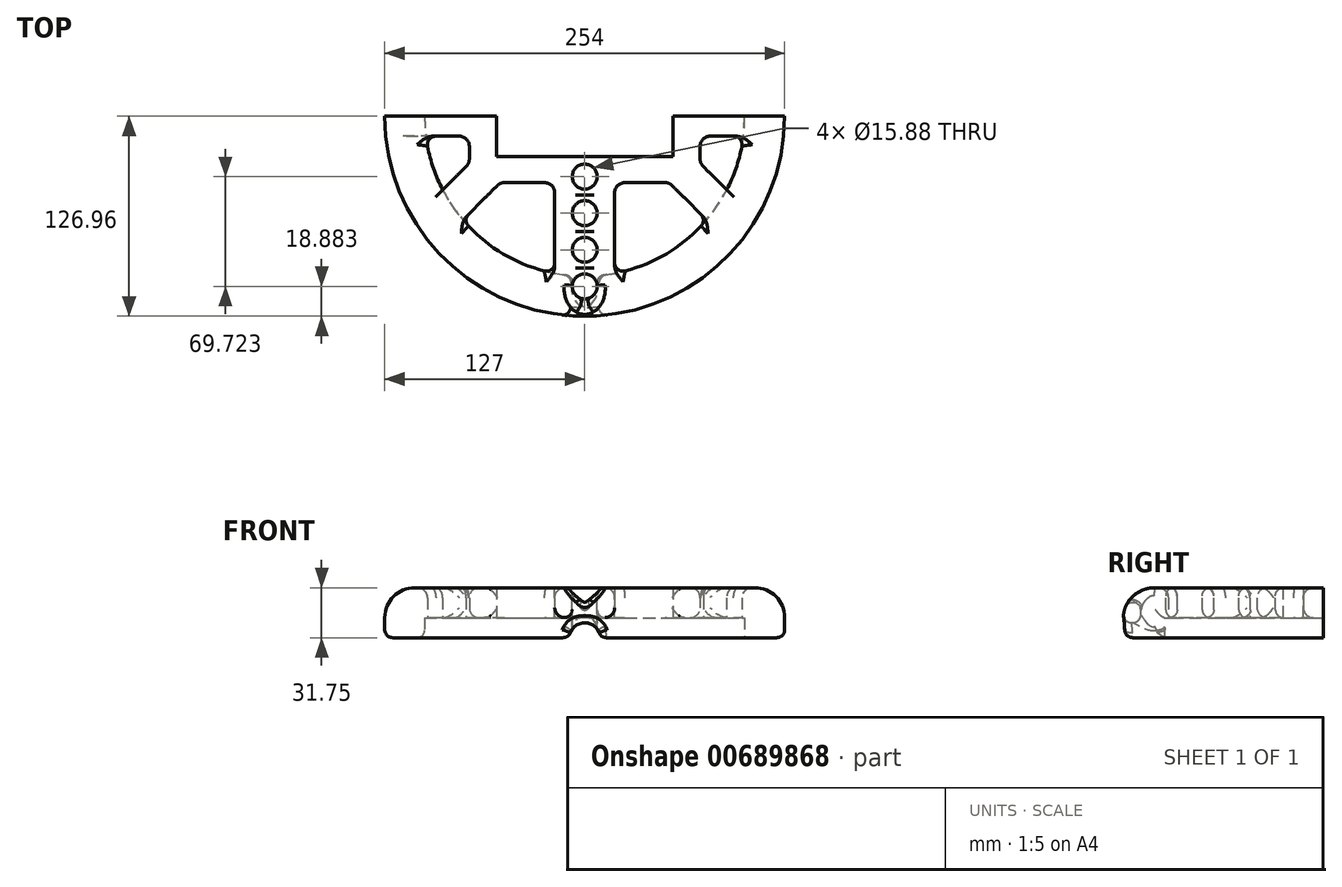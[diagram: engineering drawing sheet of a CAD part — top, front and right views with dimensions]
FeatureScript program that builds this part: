
annotation { "Feature Type Name" : "Feature", "Feature Type Description" : "" }
export const myFeature = defineFeature(function(context is Context, id is Id, definition is map)
    precondition{}
    {
        {
            var Q0;
            Q0=qCreatedBy(makeId("Top.planeOp"),FACE);
            var sketch = newSketch(context, id + "F0", { "sketchPlane" : qUnion([Q0])});
            skCircle(sketch, "E0", {"center": v(0, 0) * mm, "radius": 127 * mm});
            skCircle(sketch, "E1", {"center": v(0, 0) * mm, "radius": 101.6 * mm});
            skLineSegment(sketch, "E2", {"start": v(-127, 0) * mm, "end": v(127, 0) * mm});
            skLineSegment(sketch, "E3.bottom", {"start": v(-56.13, -25.65) * mm, "end": v(56.13, -25.65) * mm});
            skLineSegment(sketch, "E3.top", {"start": v(-56.13, 25.65) * mm, "end": v(56.13, 25.65) * mm});
            skLineSegment(sketch, "E3.left", {"start": v(-56.13, -25.65) * mm, "end": v(-56.13, 25.65) * mm});
            skLineSegment(sketch, "E3.right", {"start": v(56.13, -25.65) * mm, "end": v(56.13, 25.65) * mm});
            skLineSegment(sketch, "E4", {"start": v(-56.13, -12.7) * mm, "end": v(-100.8, -12.7) * mm});
            skLineSegment(sketch, "E5", {"start": v(0, 25.65) * mm, "end": v(0, -25.65) * mm, "construction": true});
            skLineSegment(sketch, "E6", {"start": v(0, 0) * mm, "end": v(-89.8, -89.8) * mm, "construction": true});
            skLineSegment(sketch, "E7", {"start": v(-56.13, -12.7) * mm, "end": v(-90.2, -46.76) * mm});
            skPoint(sketch, "E8", {"position": v(-37.08, -25.65) * mm});
            skLineSegment(sketch, "E9", {"start": v(-37.08, -25.65) * mm, "end": v(-77.33, -65.9) * mm});
            skLineSegment(sketch, "E10.bottom", {"start": v(-73.28, -42.16) * mm, "end": v(73.28, -42.16) * mm});
            skLineSegment(sketch, "E10.top", {"start": v(-73.28, 42.16) * mm, "end": v(73.28, 42.16) * mm});
            skLineSegment(sketch, "E10.left", {"start": v(-73.28, -42.16) * mm, "end": v(-73.28, 42.16) * mm});
            skLineSegment(sketch, "E10.right", {"start": v(73.28, -42.16) * mm, "end": v(73.28, 42.16) * mm});
            skLineSegment(sketch, "E11.MirrorCS", {"start": v(37.08, -25.65) * mm, "end": v(77.33, -65.9) * mm});
            skLineSegment(sketch, "E12.MirrorCS", {"start": v(56.13, -12.7) * mm, "end": v(90.2, -46.76) * mm});
            skLineSegment(sketch, "E13.MirrorCS", {"start": v(56.13, -12.7) * mm, "end": v(100.8, -12.7) * mm});
            skLineSegment(sketch, "E14", {"start": v(-19.05, -42.16) * mm, "end": v(-19.05, -99.8) * mm});
            skLineSegment(sketch, "E15.MirrorCS", {"start": v(19.05, -42.16) * mm, "end": v(19.05, -99.8) * mm});
            skSolve(sketch);
        }
        {
            var Q0;
            {var subQ0=sQuery(id+"F0.wireOp",EDGE,"E2");var subQ1=sQuery(id+"F0.wireOp",EDGE,"E0");var subQ2=makeQuery(id+"F0.imprint","INTERSECT",VERTEX,{"disambiguationData":[OD(0.0)],"derivedFrom":[subQ1,subQ0]});Q0=makeQuery(id+"F0.imprint","IMPRINT",FACE,{"disambiguationData":[TD([[makeQuery(id+"F0.imprint","IMPRINT",EDGE,{"disambiguationData":[TD([[subQ2,-1.0]])],"derivedFrom":subQ1}),1.0]])]});}
            var Q1;
            {var subQ0=sQuery(id+"F0.wireOp",EDGE,"E4");var subQ1=sQuery(id+"F0.wireOp",EDGE,"E1");var subQ2=makeQuery(id+"F0.imprint","INTERSECT",VERTEX,{"derivedFrom":[subQ1,subQ0]});Q1=makeQuery(id+"F0.imprint","IMPRINT",FACE,{"disambiguationData":[TD([[makeQuery(id+"F0.imprint","IMPRINT",EDGE,{"disambiguationData":[TD([[subQ2,1.0]])],"derivedFrom":subQ1}),1.0]])]});}
            var Q2;
            {var subQ0=sQuery(id+"F0.wireOp",EDGE,"E10.left");var subQ1=sQuery(id+"F0.wireOp",EDGE,"E2");var subQ2=makeQuery(id+"F0.imprint","INTERSECT",VERTEX,{"derivedFrom":[subQ1,subQ0]});Q2=makeQuery(id+"F0.imprint","IMPRINT",FACE,{"disambiguationData":[TD([[makeQuery(id+"F0.imprint","IMPRINT",EDGE,{"disambiguationData":[TD([[subQ2,-1.0]])],"derivedFrom":subQ1}),-1.0]])]});}
            var Q3;
            {var subQ1=sQuery(id+"F0.wireOp",EDGE,"E4");var subQ3=sQuery(id+"F0.wireOp",EDGE,"E10.left");var subQ4=makeQuery(id+"F0.imprint","INTERSECT",VERTEX,{"derivedFrom":[subQ1,subQ3]});Q3=makeQuery(id+"F0.imprint","IMPRINT",FACE,{"disambiguationData":[TD([[makeQuery(id+"F0.imprint","IMPRINT",EDGE,{"disambiguationData":[TD([[subQ4,1.0]])],"derivedFrom":subQ3}),-1.0]])]});}
            var Q4;
            {var subQ1=sQuery(id+"F0.wireOp",EDGE,"E3.left");var subQ6=sQuery(id+"F0.wireOp",EDGE,"E3.bottom");var subQ10=makeQuery(id+"F0.imprint","INTERSECT",VERTEX,{"derivedFrom":[subQ6,subQ1]});Q4=makeQuery(id+"F0.imprint","IMPRINT",FACE,{"disambiguationData":[TD([[makeQuery(id+"F0.imprint","IMPRINT",EDGE,{"disambiguationData":[TD([[subQ10,-1.0]])],"derivedFrom":subQ6}),-1.0]])]});}
            var Q5;
            {var subQ0=sQuery(id+"F0.wireOp",EDGE,"E9");var subQ1=sQuery(id+"F0.wireOp",EDGE,"E3.bottom");var subQ2=makeQuery(id+"F0.imprint","INTERSECT",VERTEX,{"derivedFrom":[subQ1,subQ0]});Q5=makeQuery(id+"F0.imprint","IMPRINT",FACE,{"disambiguationData":[TD([[makeQuery(id+"F0.imprint","IMPRINT",EDGE,{"disambiguationData":[TD([[subQ2,-1.0]])],"derivedFrom":subQ1}),-1.0]])]});}
            var Q6;
            {var subQ5=sQuery(id+"F0.wireOp",EDGE,"E3.right");var subQ6=sQuery(id+"F0.wireOp",EDGE,"E3.bottom");var subQ7=makeQuery(id+"F0.imprint","INTERSECT",VERTEX,{"derivedFrom":[subQ6,subQ5]});Q6=makeQuery(id+"F0.imprint","IMPRINT",FACE,{"disambiguationData":[TD([[makeQuery(id+"F0.imprint","IMPRINT",EDGE,{"disambiguationData":[TD([[subQ7,1.0]])],"derivedFrom":subQ6}),-1.0]])]});}
            var Q7;
            {var subQ0=sQuery(id+"F0.wireOp",EDGE,"E12.MirrorCS");var subQ1=sQuery(id+"F0.wireOp",EDGE,"E10.right");var subQ2=makeQuery(id+"F0.imprint","INTERSECT",VERTEX,{"derivedFrom":[subQ1,subQ0]});Q7=makeQuery(id+"F0.imprint","IMPRINT",FACE,{"disambiguationData":[TD([[makeQuery(id+"F0.imprint","IMPRINT",EDGE,{"disambiguationData":[TD([[subQ2,-1.0]])],"derivedFrom":subQ1}),1.0]])]});}
            var Q8;
            {var subQ0=sQuery(id+"F0.wireOp",EDGE,"E3.right");var subQ1=sQuery(id+"F0.wireOp",EDGE,"E2");var subQ2=makeQuery(id+"F0.imprint","INTERSECT",VERTEX,{"derivedFrom":[subQ1,subQ0]});Q8=makeQuery(id+"F0.imprint","IMPRINT",FACE,{"disambiguationData":[TD([[makeQuery(id+"F0.imprint","IMPRINT",EDGE,{"disambiguationData":[TD([[subQ2,-1.0]])],"derivedFrom":subQ1}),-1.0]])]});}
            var Q9;
            {var subQ0=sQuery(id+"F0.wireOp",EDGE,"E13.MirrorCS");var subQ1=sQuery(id+"F0.wireOp",EDGE,"E1");var subQ2=makeQuery(id+"F0.imprint","INTERSECT",VERTEX,{"derivedFrom":[subQ1,subQ0]});Q9=makeQuery(id+"F0.imprint","IMPRINT",FACE,{"disambiguationData":[TD([[makeQuery(id+"F0.imprint","IMPRINT",EDGE,{"disambiguationData":[TD([[subQ2,-1.0]])],"derivedFrom":subQ1}),1.0]])]});}
            var Q10;
            {var subQ5=sQuery(id+"F0.wireOp",EDGE,"E1");var subQ7=sQuery(id+"F0.wireOp",EDGE,"E7");var subQ8=makeQuery(id+"F0.imprint","INTERSECT",VERTEX,{"derivedFrom":[subQ5,subQ7]});Q10=makeQuery(id+"F0.imprint","IMPRINT",FACE,{"disambiguationData":[TD([[makeQuery(id+"F0.imprint","IMPRINT",EDGE,{"disambiguationData":[TD([[subQ8,-1.0]])],"derivedFrom":subQ5}),1.0]])]});}
            var Q11;
            {var subQ0=sQuery(id+"F0.wireOp",EDGE,"E11.MirrorCS");var subQ1=sQuery(id+"F0.wireOp",EDGE,"E1");var subQ2=makeQuery(id+"F0.imprint","INTERSECT",VERTEX,{"derivedFrom":[subQ1,subQ0]});Q11=makeQuery(id+"F0.imprint","IMPRINT",FACE,{"disambiguationData":[TD([[makeQuery(id+"F0.imprint","IMPRINT",EDGE,{"disambiguationData":[TD([[subQ2,-1.0]])],"derivedFrom":subQ1}),1.0]])]});}
            var Q12;
            {var subQ0=sQuery(id+"F0.wireOp",EDGE,"E14");Q12=makeQuery(id+"F0.imprint","IMPRINT",FACE,{"disambiguationData":[TD([[makeQuery(id+"F0.imprint","IMPRINT",EDGE,{"derivedFrom":subQ0}),1.0]])]});}
            extrude(context, id + "F1", {"entities" : qUnion([Q0, Q1, Q2, Q3, Q4, Q5, Q6, Q7, Q8, Q9, Q10, Q11, Q12]), "depth" : 31.75 * mm, "offsetDistance" : 25.4 * mm});
        }
        {
            var Q0;
            Q0=qCreatedBy(makeId("Front.planeOp"),FACE);
            cPlane(context, id + "F2", {"entities" : qUnion([Q0]), "cplaneType" : CPlaneType.OFFSET, "offset" : 139.7 * mm, "width" : 152.4 * mm, "height" : 152.4 * mm});
        }
        {
            var Q0;
            Q0=qCreatedBy(id+"F2.planeOp",FACE);
            var sketch = newSketch(context, id + "F3", { "sketchPlane" : qUnion([Q0])});
            skCircle(sketch, "E16", {"center": v(0, 0) * mm, "radius": 9.53 * mm});
            skSolve(sketch);
        }
        {
            var Q0;
            Q0=makeQuery(id+"F3.imprint","IMPRINT",FACE,{"disambiguationData":[TD([[makeQuery(id+"F3.imprint","IMPRINT",EDGE,{"derivedFrom":sQuery(id+"F3.wireOp",EDGE,"E16")}),1.0]])]});
            extrude(context, id + "F4", {"entities" : qUnion([Q0]), "operationType" : NewBodyOperationType.REMOVE, "oppositeDirection" : true, "depth" : 44.45 * mm, "offsetDistance" : 25.4 * mm});
        }
        {
            var Q0;
            {var subQ0=sQuery(id+"F0.wireOp",EDGE,"E14");Q0=makeQuery(id+"F0.imprint","IMPRINT",FACE,{"disambiguationData":[TD([[makeQuery(id+"F0.imprint","IMPRINT",EDGE,{"derivedFrom":subQ0}),1.0]])]});}
            var Q1;
            {var subQ0=sQuery(id+"F0.wireOp",EDGE,"E11.MirrorCS");var subQ1=sQuery(id+"F0.wireOp",EDGE,"E1");var subQ2=makeQuery(id+"F0.imprint","INTERSECT",VERTEX,{"derivedFrom":[subQ1,subQ0]});Q1=makeQuery(id+"F0.imprint","IMPRINT",FACE,{"disambiguationData":[TD([[makeQuery(id+"F0.imprint","IMPRINT",EDGE,{"disambiguationData":[TD([[subQ2,-1.0]])],"derivedFrom":subQ1}),1.0]])]});}
            var Q2;
            {var subQ7=sQuery(id+"F0.wireOp",EDGE,"E3.right");var subQ8=sQuery(id+"F0.wireOp",EDGE,"E3.bottom");var subQ9=makeQuery(id+"F0.imprint","INTERSECT",VERTEX,{"derivedFrom":[subQ8,subQ7]});Q2=makeQuery(id+"F0.imprint","IMPRINT",FACE,{"disambiguationData":[TD([[makeQuery(id+"F0.imprint","IMPRINT",EDGE,{"disambiguationData":[TD([[subQ9,1.0]])],"derivedFrom":subQ8}),-1.0]])]});}
            var Q3;
            {var subQ0=sQuery(id+"F0.wireOp",EDGE,"E12.MirrorCS");var subQ1=sQuery(id+"F0.wireOp",EDGE,"E10.right");var subQ2=makeQuery(id+"F0.imprint","INTERSECT",VERTEX,{"derivedFrom":[subQ1,subQ0]});Q3=makeQuery(id+"F0.imprint","IMPRINT",FACE,{"disambiguationData":[TD([[makeQuery(id+"F0.imprint","IMPRINT",EDGE,{"disambiguationData":[TD([[subQ2,-1.0]])],"derivedFrom":subQ1}),1.0]])]});}
            var Q4;
            {var subQ0=sQuery(id+"F0.wireOp",EDGE,"E3.right");var subQ1=sQuery(id+"F0.wireOp",EDGE,"E2");var subQ2=makeQuery(id+"F0.imprint","INTERSECT",VERTEX,{"derivedFrom":[subQ1,subQ0]});Q4=makeQuery(id+"F0.imprint","IMPRINT",FACE,{"disambiguationData":[TD([[makeQuery(id+"F0.imprint","IMPRINT",EDGE,{"disambiguationData":[TD([[subQ2,-1.0]])],"derivedFrom":subQ1}),-1.0]])]});}
            var Q5;
            {var subQ0=sQuery(id+"F0.wireOp",EDGE,"E13.MirrorCS");var subQ1=sQuery(id+"F0.wireOp",EDGE,"E1");var subQ2=makeQuery(id+"F0.imprint","INTERSECT",VERTEX,{"derivedFrom":[subQ1,subQ0]});Q5=makeQuery(id+"F0.imprint","IMPRINT",FACE,{"disambiguationData":[TD([[makeQuery(id+"F0.imprint","IMPRINT",EDGE,{"disambiguationData":[TD([[subQ2,-1.0]])],"derivedFrom":subQ1}),1.0]])]});}
            var Q6;
            {var subQ3=sQuery(id+"F0.wireOp",EDGE,"E9");var subQ5=sQuery(id+"F0.wireOp",EDGE,"E3.bottom");var subQ6=makeQuery(id+"F0.imprint","INTERSECT",VERTEX,{"derivedFrom":[subQ5,subQ3]});Q6=makeQuery(id+"F0.imprint","IMPRINT",FACE,{"disambiguationData":[TD([[makeQuery(id+"F0.imprint","IMPRINT",EDGE,{"disambiguationData":[TD([[subQ6,-1.0]])],"derivedFrom":subQ5}),-1.0]])]});}
            var Q7;
            {var subQ1=sQuery(id+"F0.wireOp",EDGE,"E3.left");var subQ6=sQuery(id+"F0.wireOp",EDGE,"E3.bottom");var subQ10=makeQuery(id+"F0.imprint","INTERSECT",VERTEX,{"derivedFrom":[subQ6,subQ1]});Q7=makeQuery(id+"F0.imprint","IMPRINT",FACE,{"disambiguationData":[TD([[makeQuery(id+"F0.imprint","IMPRINT",EDGE,{"disambiguationData":[TD([[subQ10,-1.0]])],"derivedFrom":subQ6}),-1.0]])]});}
            var Q8;
            {var subQ1=sQuery(id+"F0.wireOp",EDGE,"E1");var subQ5=sQuery(id+"F0.wireOp",EDGE,"E7");var subQ6=makeQuery(id+"F0.imprint","INTERSECT",VERTEX,{"derivedFrom":[subQ1,subQ5]});Q8=makeQuery(id+"F0.imprint","IMPRINT",FACE,{"disambiguationData":[TD([[makeQuery(id+"F0.imprint","IMPRINT",EDGE,{"disambiguationData":[TD([[subQ6,-1.0]])],"derivedFrom":subQ1}),1.0]])]});}
            var Q9;
            {var subQ0=sQuery(id+"F0.wireOp",EDGE,"E4");var subQ1=sQuery(id+"F0.wireOp",EDGE,"E1");var subQ2=makeQuery(id+"F0.imprint","INTERSECT",VERTEX,{"derivedFrom":[subQ1,subQ0]});Q9=makeQuery(id+"F0.imprint","IMPRINT",FACE,{"disambiguationData":[TD([[makeQuery(id+"F0.imprint","IMPRINT",EDGE,{"disambiguationData":[TD([[subQ2,1.0]])],"derivedFrom":subQ1}),1.0]])]});}
            var Q10;
            {var subQ1=sQuery(id+"F0.wireOp",EDGE,"E4");var subQ3=sQuery(id+"F0.wireOp",EDGE,"E10.left");var subQ4=makeQuery(id+"F0.imprint","INTERSECT",VERTEX,{"derivedFrom":[subQ1,subQ3]});Q10=makeQuery(id+"F0.imprint","IMPRINT",FACE,{"disambiguationData":[TD([[makeQuery(id+"F0.imprint","IMPRINT",EDGE,{"disambiguationData":[TD([[subQ4,1.0]])],"derivedFrom":subQ3}),-1.0]])]});}
            var Q11;
            {var subQ0=sQuery(id+"F0.wireOp",EDGE,"E10.left");var subQ1=sQuery(id+"F0.wireOp",EDGE,"E2");var subQ2=makeQuery(id+"F0.imprint","INTERSECT",VERTEX,{"derivedFrom":[subQ1,subQ0]});Q11=makeQuery(id+"F0.imprint","IMPRINT",FACE,{"disambiguationData":[TD([[makeQuery(id+"F0.imprint","IMPRINT",EDGE,{"disambiguationData":[TD([[subQ2,-1.0]])],"derivedFrom":subQ1}),-1.0]])]});}
            extrude(context, id + "F5", {"entities" : qUnion([Q0, Q1, Q2, Q3, Q4, Q5, Q6, Q7, Q8, Q9, Q10, Q11]), "operationType" : NewBodyOperationType.REMOVE, "depth" : 12.7 * mm, "offsetDistance" : 25.4 * mm});
        }
        {
            var Q0;
            Q0=makeQuery(id+"FQLxLcLUYKDh7PT_1.6.F4.boolean.opBoolean","COPY",FACE,{"derivedFrom":makeQuery(id+"FQLxLcLUYKDh7PT_1.6.F4.opExtrude","SWEPT_FACE",FACE,{"disambiguationData":[OSD([sQuery(id+"F3.wireOp",EDGE,"E16")])]})});
            var Q1;
            Q1=makeQuery(id+"FQLxLcLUYKDh7PT_1.7.F4.boolean.opBoolean","COPY",FACE,{"derivedFrom":makeQuery(id+"FQLxLcLUYKDh7PT_1.7.F4.opExtrude","SWEPT_FACE",FACE,{"disambiguationData":[OSD([sQuery(id+"F3.wireOp",EDGE,"E16")])]})});
            var Q2;
            Q2=makeQuery(id+"FQLxLcLUYKDh7PT_1.5.F4.boolean.opBoolean","COPY",FACE,{"derivedFrom":makeQuery(id+"FQLxLcLUYKDh7PT_1.5.F4.opExtrude","SWEPT_FACE",FACE,{"disambiguationData":[OSD([sQuery(id+"F3.wireOp",EDGE,"E16")])]})});
            var Q3;
            Q3=makeQuery(id+"FQLxLcLUYKDh7PT_1.4.F4.boolean.opBoolean","COPY",FACE,{"derivedFrom":makeQuery(id+"FQLxLcLUYKDh7PT_1.4.F4.opExtrude","SWEPT_FACE",FACE,{"disambiguationData":[OSD([sQuery(id+"F3.wireOp",EDGE,"E16")])]})});
            var Q4;
            Q4=makeQuery(id+"FQLxLcLUYKDh7PT_1.3.F4.boolean.opBoolean","COPY",FACE,{"derivedFrom":makeQuery(id+"FQLxLcLUYKDh7PT_1.3.F4.opExtrude","SWEPT_FACE",FACE,{"disambiguationData":[OSD([sQuery(id+"F3.wireOp",EDGE,"E16")])]})});
            var Q5;
            Q5=makeQuery(id+"FQLxLcLUYKDh7PT_1.2.F4.boolean.opBoolean","COPY",FACE,{"derivedFrom":makeQuery(id+"FQLxLcLUYKDh7PT_1.2.F4.opExtrude","SWEPT_FACE",FACE,{"disambiguationData":[OSD([sQuery(id+"F3.wireOp",EDGE,"E16")])]})});
            var Q6;
            Q6=makeQuery(id+"FQLxLcLUYKDh7PT_1.1.F4.boolean.opBoolean","COPY",FACE,{"derivedFrom":makeQuery(id+"FQLxLcLUYKDh7PT_1.1.F4.opExtrude","SWEPT_FACE",FACE,{"disambiguationData":[OSD([sQuery(id+"F3.wireOp",EDGE,"E16")])]})});
            var Q7;
            Q7=makeQuery(id+"F4.boolean.opBoolean","COPY",FACE,{"derivedFrom":makeQuery(id+"F4.opExtrude","SWEPT_FACE",FACE,{"disambiguationData":[OSD([sQuery(id+"F3.wireOp",EDGE,"E16")])]})});
            var Q8;
            Q8=makeQuery(id+"FQLxLcLUYKDh7PT_1.-1.F4.boolean.opBoolean","COPY",FACE,{"derivedFrom":makeQuery(id+"FQLxLcLUYKDh7PT_1.-1.F4.opExtrude","SWEPT_FACE",FACE,{"disambiguationData":[OSD([sQuery(id+"F3.wireOp",EDGE,"E16")])]})});
            var Q9;
            Q9=makeQuery(id+"FQLxLcLUYKDh7PT_1.-2.F4.boolean.opBoolean","COPY",FACE,{"derivedFrom":makeQuery(id+"FQLxLcLUYKDh7PT_1.-2.F4.opExtrude","SWEPT_FACE",FACE,{"disambiguationData":[OSD([sQuery(id+"F3.wireOp",EDGE,"E16")])]})});
            var Q10;
            Q10=makeQuery(id+"FQLxLcLUYKDh7PT_1.-3.F4.boolean.opBoolean","COPY",FACE,{"derivedFrom":makeQuery(id+"FQLxLcLUYKDh7PT_1.-3.F4.opExtrude","SWEPT_FACE",FACE,{"disambiguationData":[OSD([sQuery(id+"F3.wireOp",EDGE,"E16")])]})});
            var Q11;
            Q11=makeQuery(id+"FQLxLcLUYKDh7PT_1.-4.F4.boolean.opBoolean","COPY",FACE,{"derivedFrom":makeQuery(id+"FQLxLcLUYKDh7PT_1.-4.F4.opExtrude","SWEPT_FACE",FACE,{"disambiguationData":[OSD([sQuery(id+"F3.wireOp",EDGE,"E16")])]})});
            var Q12;
            Q12=makeQuery(id+"FQLxLcLUYKDh7PT_1.-5.F4.boolean.opBoolean","COPY",FACE,{"derivedFrom":makeQuery(id+"FQLxLcLUYKDh7PT_1.-5.F4.opExtrude","SWEPT_FACE",FACE,{"disambiguationData":[OSD([sQuery(id+"F3.wireOp",EDGE,"E16")])]})});
            var Q13;
            Q13=makeQuery(id+"FQLxLcLUYKDh7PT_1.-6.F4.boolean.opBoolean","COPY",FACE,{"derivedFrom":makeQuery(id+"FQLxLcLUYKDh7PT_1.-6.F4.opExtrude","SWEPT_FACE",FACE,{"disambiguationData":[OSD([sQuery(id+"F3.wireOp",EDGE,"E16")])]})});
            var Q14;
            Q14=makeQuery(id+"FQLxLcLUYKDh7PT_1.-7.F4.boolean.opBoolean","COPY",FACE,{"derivedFrom":makeQuery(id+"FQLxLcLUYKDh7PT_1.-7.F4.opExtrude","SWEPT_FACE",FACE,{"disambiguationData":[OSD([sQuery(id+"F3.wireOp",EDGE,"E16")])]})});
            var Q15;
            {var subQ0=sQuery(id+"F0.wireOp",EDGE,"E0");var subQ3=sQuery(id+"F0.wireOp",EDGE,"E10.left");var subQ5=sQuery(id+"F0.wireOp",EDGE,"E2");var subQ6=sQuery(id+"F0.wireOp",EDGE,"E1");var subQ8=makeQuery(id+"F0.imprint","INTERSECT",VERTEX,{"derivedFrom":[subQ5,subQ3]});var subQ9=makeQuery(id+"F0.imprint","INTERSECT",VERTEX,{"disambiguationData":[OD(0.0)],"derivedFrom":[subQ6,subQ5]});var subQ10=makeQuery(id+"F1.opExtrude","SWEPT_FACE",FACE,{"disambiguationData":[OSD([subQ5]),TDD([makeQuery(id+"F0.imprint","IMPRINT",EDGE,{"disambiguationData":[TD([[makeQuery(id+"F0.imprint","INTERSECT",VERTEX,{"disambiguationData":[OD(0.0)],"derivedFrom":[subQ0,subQ5]}),-1.0]])],"derivedFrom":subQ5}),makeQuery(id+"F0.imprint","IMPRINT",EDGE,{"disambiguationData":[TD([[subQ9,-1.0]])],"derivedFrom":subQ5}),makeQuery(id+"F0.imprint","IMPRINT",EDGE,{"disambiguationData":[TD([[subQ8,-1.0]])],"derivedFrom":subQ5})])]});Q15=makeQuery(id+"FQLxLcLUYKDh7PT_1.-5.F4.boolean.opBoolean","SPLIT",EDGE,{"disambiguationData":[TD([subQ10])],"derivedFrom":makeQuery(id+"F4.boolean.opBoolean","SPLIT",EDGE,{"disambiguationData":[TD([subQ10])],"derivedFrom":makeQuery(id+"F1.opExtrude","CAP_EDGE",EDGE,{"disambiguationData":[OSD([subQ0])],"isStart":true})})});}
            var Q16;
            {var subQ0=sQuery(id+"F0.wireOp",EDGE,"E0");var subQ2=sQuery(id+"F0.wireOp",EDGE,"E10.left");var subQ4=sQuery(id+"F0.wireOp",EDGE,"E2");var subQ5=sQuery(id+"F0.wireOp",EDGE,"E1");var subQ7=sQuery(id+"F3.wireOp",EDGE,"E16");var subQ8=makeQuery(id+"FQLxLcLUYKDh7PT_1.-5.F4.opExtrude","SWEPT_FACE",FACE,{"disambiguationData":[OSD([subQ7])]});var subQ9=makeQuery(id+"F4.opExtrude","SWEPT_FACE",FACE,{"disambiguationData":[OSD([subQ7])]});var subQ10=makeQuery(id+"F0.imprint","INTERSECT",VERTEX,{"derivedFrom":[subQ4,subQ2]});var subQ11=makeQuery(id+"F0.imprint","INTERSECT",VERTEX,{"disambiguationData":[OD(0.0)],"derivedFrom":[subQ5,subQ4]});Q16=makeQuery(id+"FQLxLcLUYKDh7PT_1.-4.F4.boolean.opBoolean","SPLIT",EDGE,{"disambiguationData":[TD([makeQuery(id+"FQLxLcLUYKDh7PT_1.-5.F4.boolean.opBoolean","COPY",FACE,{"derivedFrom":subQ8})])],"derivedFrom":makeQuery(id+"FQLxLcLUYKDh7PT_1.-5.F4.boolean.opBoolean","SPLIT",EDGE,{"disambiguationData":[TD([makeQuery(id+"F4.boolean.opBoolean","COPY",FACE,{"derivedFrom":subQ9})])],"derivedFrom":makeQuery(id+"F4.boolean.opBoolean","SPLIT",EDGE,{"disambiguationData":[TD([makeQuery(id+"F1.opExtrude","SWEPT_FACE",FACE,{"disambiguationData":[OSD([subQ4]),TDD([makeQuery(id+"F0.imprint","IMPRINT",EDGE,{"disambiguationData":[TD([[makeQuery(id+"F0.imprint","INTERSECT",VERTEX,{"disambiguationData":[OD(0.0)],"derivedFrom":[subQ0,subQ4]}),-1.0]])],"derivedFrom":subQ4}),makeQuery(id+"F0.imprint","IMPRINT",EDGE,{"disambiguationData":[TD([[subQ11,-1.0]])],"derivedFrom":subQ4}),makeQuery(id+"F0.imprint","IMPRINT",EDGE,{"disambiguationData":[TD([[subQ10,-1.0]])],"derivedFrom":subQ4})])]})])],"derivedFrom":makeQuery(id+"F1.opExtrude","CAP_EDGE",EDGE,{"disambiguationData":[OSD([subQ0])],"isStart":true})})})});}
            var Q17;
            {var subQ0=sQuery(id+"F0.wireOp",EDGE,"E0");var subQ2=sQuery(id+"F0.wireOp",EDGE,"E10.left");var subQ4=sQuery(id+"F0.wireOp",EDGE,"E2");var subQ5=sQuery(id+"F0.wireOp",EDGE,"E1");var subQ7=sQuery(id+"F3.wireOp",EDGE,"E16");var subQ8=makeQuery(id+"FQLxLcLUYKDh7PT_1.-4.F4.opExtrude","SWEPT_FACE",FACE,{"disambiguationData":[OSD([subQ7])]});var subQ9=makeQuery(id+"F4.opExtrude","SWEPT_FACE",FACE,{"disambiguationData":[OSD([subQ7])]});var subQ10=makeQuery(id+"F4.boolean.opBoolean","COPY",FACE,{"derivedFrom":subQ9});var subQ11=makeQuery(id+"F0.imprint","INTERSECT",VERTEX,{"derivedFrom":[subQ4,subQ2]});var subQ12=makeQuery(id+"F0.imprint","INTERSECT",VERTEX,{"disambiguationData":[OD(0.0)],"derivedFrom":[subQ5,subQ4]});Q17=makeQuery(id+"FQLxLcLUYKDh7PT_1.-3.F4.boolean.opBoolean","SPLIT",EDGE,{"disambiguationData":[TD([makeQuery(id+"FQLxLcLUYKDh7PT_1.-4.F4.boolean.opBoolean","COPY",FACE,{"derivedFrom":subQ8})])],"derivedFrom":makeQuery(id+"FQLxLcLUYKDh7PT_1.-4.F4.boolean.opBoolean","SPLIT",EDGE,{"disambiguationData":[TD([subQ10])],"derivedFrom":makeQuery(id+"FQLxLcLUYKDh7PT_1.-5.F4.boolean.opBoolean","SPLIT",EDGE,{"disambiguationData":[TD([subQ10])],"derivedFrom":makeQuery(id+"F4.boolean.opBoolean","SPLIT",EDGE,{"disambiguationData":[TD([makeQuery(id+"F1.opExtrude","SWEPT_FACE",FACE,{"disambiguationData":[OSD([subQ4]),TDD([makeQuery(id+"F0.imprint","IMPRINT",EDGE,{"disambiguationData":[TD([[makeQuery(id+"F0.imprint","INTERSECT",VERTEX,{"disambiguationData":[OD(0.0)],"derivedFrom":[subQ0,subQ4]}),-1.0]])],"derivedFrom":subQ4}),makeQuery(id+"F0.imprint","IMPRINT",EDGE,{"disambiguationData":[TD([[subQ12,-1.0]])],"derivedFrom":subQ4}),makeQuery(id+"F0.imprint","IMPRINT",EDGE,{"disambiguationData":[TD([[subQ11,-1.0]])],"derivedFrom":subQ4})])]})])],"derivedFrom":makeQuery(id+"F1.opExtrude","CAP_EDGE",EDGE,{"disambiguationData":[OSD([subQ0])],"isStart":true})})})})});}
            var Q18;
            {var subQ0=sQuery(id+"F0.wireOp",EDGE,"E0");var subQ2=sQuery(id+"F3.wireOp",EDGE,"E16");var subQ3=makeQuery(id+"FQLxLcLUYKDh7PT_1.-3.F4.opExtrude","SWEPT_FACE",FACE,{"disambiguationData":[OSD([subQ2])]});var subQ4=sQuery(id+"F0.wireOp",EDGE,"E10.left");var subQ6=sQuery(id+"F0.wireOp",EDGE,"E2");var subQ7=sQuery(id+"F0.wireOp",EDGE,"E1");var subQ9=makeQuery(id+"F4.opExtrude","SWEPT_FACE",FACE,{"disambiguationData":[OSD([subQ2])]});var subQ10=makeQuery(id+"F4.boolean.opBoolean","COPY",FACE,{"derivedFrom":subQ9});var subQ11=makeQuery(id+"F0.imprint","INTERSECT",VERTEX,{"derivedFrom":[subQ6,subQ4]});var subQ12=makeQuery(id+"F0.imprint","INTERSECT",VERTEX,{"disambiguationData":[OD(0.0)],"derivedFrom":[subQ7,subQ6]});Q18=makeQuery(id+"FQLxLcLUYKDh7PT_1.-2.F4.boolean.opBoolean","SPLIT",EDGE,{"disambiguationData":[TD([makeQuery(id+"FQLxLcLUYKDh7PT_1.-3.F4.boolean.opBoolean","COPY",FACE,{"derivedFrom":subQ3})])],"derivedFrom":makeQuery(id+"FQLxLcLUYKDh7PT_1.-3.F4.boolean.opBoolean","SPLIT",EDGE,{"disambiguationData":[TD([subQ10])],"derivedFrom":makeQuery(id+"FQLxLcLUYKDh7PT_1.-4.F4.boolean.opBoolean","SPLIT",EDGE,{"disambiguationData":[TD([subQ10])],"derivedFrom":makeQuery(id+"FQLxLcLUYKDh7PT_1.-5.F4.boolean.opBoolean","SPLIT",EDGE,{"disambiguationData":[TD([subQ10])],"derivedFrom":makeQuery(id+"F4.boolean.opBoolean","SPLIT",EDGE,{"disambiguationData":[TD([makeQuery(id+"F1.opExtrude","SWEPT_FACE",FACE,{"disambiguationData":[OSD([subQ6]),TDD([makeQuery(id+"F0.imprint","IMPRINT",EDGE,{"disambiguationData":[TD([[makeQuery(id+"F0.imprint","INTERSECT",VERTEX,{"disambiguationData":[OD(0.0)],"derivedFrom":[subQ0,subQ6]}),-1.0]])],"derivedFrom":subQ6}),makeQuery(id+"F0.imprint","IMPRINT",EDGE,{"disambiguationData":[TD([[subQ12,-1.0]])],"derivedFrom":subQ6}),makeQuery(id+"F0.imprint","IMPRINT",EDGE,{"disambiguationData":[TD([[subQ11,-1.0]])],"derivedFrom":subQ6})])]})])],"derivedFrom":makeQuery(id+"F1.opExtrude","CAP_EDGE",EDGE,{"disambiguationData":[OSD([subQ0])],"isStart":true})})})})})});}
            var Q19;
            {var subQ0=sQuery(id+"F0.wireOp",EDGE,"E0");var subQ2=sQuery(id+"F0.wireOp",EDGE,"E10.left");var subQ4=sQuery(id+"F0.wireOp",EDGE,"E2");var subQ5=sQuery(id+"F0.wireOp",EDGE,"E1");var subQ7=sQuery(id+"F3.wireOp",EDGE,"E16");var subQ8=makeQuery(id+"FQLxLcLUYKDh7PT_1.-2.F4.opExtrude","SWEPT_FACE",FACE,{"disambiguationData":[OSD([subQ7])]});var subQ9=makeQuery(id+"F4.opExtrude","SWEPT_FACE",FACE,{"disambiguationData":[OSD([subQ7])]});var subQ10=makeQuery(id+"F4.boolean.opBoolean","COPY",FACE,{"derivedFrom":subQ9});var subQ11=makeQuery(id+"F0.imprint","INTERSECT",VERTEX,{"derivedFrom":[subQ4,subQ2]});var subQ12=makeQuery(id+"F0.imprint","INTERSECT",VERTEX,{"disambiguationData":[OD(0.0)],"derivedFrom":[subQ5,subQ4]});Q19=makeQuery(id+"FQLxLcLUYKDh7PT_1.-1.F4.boolean.opBoolean","SPLIT",EDGE,{"disambiguationData":[TD([makeQuery(id+"FQLxLcLUYKDh7PT_1.-2.F4.boolean.opBoolean","COPY",FACE,{"derivedFrom":subQ8})])],"derivedFrom":makeQuery(id+"FQLxLcLUYKDh7PT_1.-2.F4.boolean.opBoolean","SPLIT",EDGE,{"disambiguationData":[TD([subQ10])],"derivedFrom":makeQuery(id+"FQLxLcLUYKDh7PT_1.-3.F4.boolean.opBoolean","SPLIT",EDGE,{"disambiguationData":[TD([subQ10])],"derivedFrom":makeQuery(id+"FQLxLcLUYKDh7PT_1.-4.F4.boolean.opBoolean","SPLIT",EDGE,{"disambiguationData":[TD([subQ10])],"derivedFrom":makeQuery(id+"FQLxLcLUYKDh7PT_1.-5.F4.boolean.opBoolean","SPLIT",EDGE,{"disambiguationData":[TD([subQ10])],"derivedFrom":makeQuery(id+"F4.boolean.opBoolean","SPLIT",EDGE,{"disambiguationData":[TD([makeQuery(id+"F1.opExtrude","SWEPT_FACE",FACE,{"disambiguationData":[OSD([subQ4]),TDD([makeQuery(id+"F0.imprint","IMPRINT",EDGE,{"disambiguationData":[TD([[makeQuery(id+"F0.imprint","INTERSECT",VERTEX,{"disambiguationData":[OD(0.0)],"derivedFrom":[subQ0,subQ4]}),-1.0]])],"derivedFrom":subQ4}),makeQuery(id+"F0.imprint","IMPRINT",EDGE,{"disambiguationData":[TD([[subQ12,-1.0]])],"derivedFrom":subQ4}),makeQuery(id+"F0.imprint","IMPRINT",EDGE,{"disambiguationData":[TD([[subQ11,-1.0]])],"derivedFrom":subQ4})])]})])],"derivedFrom":makeQuery(id+"F1.opExtrude","CAP_EDGE",EDGE,{"disambiguationData":[OSD([subQ0])],"isStart":true})})})})})})});}
            var Q20;
            {var subQ0=sQuery(id+"F0.wireOp",EDGE,"E0");var subQ2=sQuery(id+"F3.wireOp",EDGE,"E16");var subQ3=makeQuery(id+"F4.opExtrude","SWEPT_FACE",FACE,{"disambiguationData":[OSD([subQ2])]});var subQ4=makeQuery(id+"F4.boolean.opBoolean","COPY",FACE,{"derivedFrom":subQ3});var subQ5=sQuery(id+"F0.wireOp",EDGE,"E10.left");var subQ7=sQuery(id+"F0.wireOp",EDGE,"E2");var subQ8=sQuery(id+"F0.wireOp",EDGE,"E1");var subQ10=makeQuery(id+"F0.imprint","INTERSECT",VERTEX,{"derivedFrom":[subQ7,subQ5]});var subQ11=makeQuery(id+"F0.imprint","INTERSECT",VERTEX,{"disambiguationData":[OD(0.0)],"derivedFrom":[subQ8,subQ7]});Q20=makeQuery(id+"FQLxLcLUYKDh7PT_1.-1.F4.boolean.opBoolean","SPLIT",EDGE,{"disambiguationData":[TD([subQ4])],"derivedFrom":makeQuery(id+"FQLxLcLUYKDh7PT_1.-2.F4.boolean.opBoolean","SPLIT",EDGE,{"disambiguationData":[TD([subQ4])],"derivedFrom":makeQuery(id+"FQLxLcLUYKDh7PT_1.-3.F4.boolean.opBoolean","SPLIT",EDGE,{"disambiguationData":[TD([subQ4])],"derivedFrom":makeQuery(id+"FQLxLcLUYKDh7PT_1.-4.F4.boolean.opBoolean","SPLIT",EDGE,{"disambiguationData":[TD([subQ4])],"derivedFrom":makeQuery(id+"FQLxLcLUYKDh7PT_1.-5.F4.boolean.opBoolean","SPLIT",EDGE,{"disambiguationData":[TD([subQ4])],"derivedFrom":makeQuery(id+"F4.boolean.opBoolean","SPLIT",EDGE,{"disambiguationData":[TD([makeQuery(id+"F1.opExtrude","SWEPT_FACE",FACE,{"disambiguationData":[OSD([subQ7]),TDD([makeQuery(id+"F0.imprint","IMPRINT",EDGE,{"disambiguationData":[TD([[makeQuery(id+"F0.imprint","INTERSECT",VERTEX,{"disambiguationData":[OD(0.0)],"derivedFrom":[subQ0,subQ7]}),-1.0]])],"derivedFrom":subQ7}),makeQuery(id+"F0.imprint","IMPRINT",EDGE,{"disambiguationData":[TD([[subQ11,-1.0]])],"derivedFrom":subQ7}),makeQuery(id+"F0.imprint","IMPRINT",EDGE,{"disambiguationData":[TD([[subQ10,-1.0]])],"derivedFrom":subQ7})])]})])],"derivedFrom":makeQuery(id+"F1.opExtrude","CAP_EDGE",EDGE,{"disambiguationData":[OSD([subQ0])],"isStart":true})})})})})})});}
            var Q21;
            {var subQ0=sQuery(id+"F0.wireOp",EDGE,"E0");var subQ2=sQuery(id+"F3.wireOp",EDGE,"E16");var subQ3=makeQuery(id+"F4.opExtrude","SWEPT_FACE",FACE,{"disambiguationData":[OSD([subQ2])]});var subQ5=sQuery(id+"F0.wireOp",EDGE,"E3.right");var subQ6=sQuery(id+"F0.wireOp",EDGE,"E2");var subQ7=sQuery(id+"F0.wireOp",EDGE,"E1");var subQ9=makeQuery(id+"F0.imprint","INTERSECT",VERTEX,{"disambiguationData":[OD(1.0)],"derivedFrom":[subQ7,subQ6]});Q21=makeQuery(id+"FQLxLcLUYKDh7PT_1.1.F4.boolean.opBoolean","SPLIT",EDGE,{"disambiguationData":[TD([makeQuery(id+"F4.boolean.opBoolean","COPY",FACE,{"derivedFrom":subQ3})])],"derivedFrom":makeQuery(id+"F4.boolean.opBoolean","SPLIT",EDGE,{"disambiguationData":[TD([makeQuery(id+"F1.opExtrude","SWEPT_FACE",FACE,{"disambiguationData":[OSD([subQ6]),TDD([makeQuery(id+"F0.imprint","IMPRINT",EDGE,{"disambiguationData":[TD([[makeQuery(id+"F0.imprint","INTERSECT",VERTEX,{"derivedFrom":[subQ6,subQ5]}),-1.0]])],"derivedFrom":subQ6}),makeQuery(id+"F0.imprint","IMPRINT",EDGE,{"disambiguationData":[TD([[subQ9,1.0]])],"derivedFrom":subQ6}),makeQuery(id+"F0.imprint","IMPRINT",EDGE,{"disambiguationData":[TD([[makeQuery(id+"F0.imprint","INTERSECT",VERTEX,{"disambiguationData":[OD(1.0)],"derivedFrom":[subQ0,subQ6]}),1.0]])],"derivedFrom":subQ6})])]})])],"derivedFrom":makeQuery(id+"F1.opExtrude","CAP_EDGE",EDGE,{"disambiguationData":[OSD([subQ0])],"isStart":true})})});}
            var Q22;
            {var subQ0=sQuery(id+"F0.wireOp",EDGE,"E0");var subQ1=makeQuery(id+"F1.opExtrude","SWEPT_FACE",FACE,{"disambiguationData":[OSD([subQ0])]});var subQ5=sQuery(id+"F0.wireOp",EDGE,"E3.right");var subQ6=sQuery(id+"F0.wireOp",EDGE,"E2");var subQ7=sQuery(id+"F0.wireOp",EDGE,"E1");var subQ9=sQuery(id+"F3.wireOp",EDGE,"E16");var subQ10=makeQuery(id+"FQLxLcLUYKDh7PT_1.1.F4.opExtrude","SWEPT_FACE",FACE,{"disambiguationData":[OSD([subQ9])]});var subQ11=makeQuery(id+"F0.imprint","INTERSECT",VERTEX,{"disambiguationData":[OD(1.0)],"derivedFrom":[subQ7,subQ6]});var subQ13=makeQuery(id+"F1.opExtrude","SWEPT_FACE",FACE,{"disambiguationData":[OSD([subQ6]),TDD([makeQuery(id+"F0.imprint","IMPRINT",EDGE,{"disambiguationData":[TD([[makeQuery(id+"F0.imprint","INTERSECT",VERTEX,{"derivedFrom":[subQ6,subQ5]}),-1.0]])],"derivedFrom":subQ6}),makeQuery(id+"F0.imprint","IMPRINT",EDGE,{"disambiguationData":[TD([[subQ11,1.0]])],"derivedFrom":subQ6}),makeQuery(id+"F0.imprint","IMPRINT",EDGE,{"disambiguationData":[TD([[makeQuery(id+"F0.imprint","INTERSECT",VERTEX,{"disambiguationData":[OD(1.0)],"derivedFrom":[subQ0,subQ6]}),1.0]])],"derivedFrom":subQ6})])]});Q22=makeQuery(id+"FQLxLcLUYKDh7PT_1.2.F4.boolean.opBoolean","SPLIT",EDGE,{"disambiguationData":[TD([makeQuery(id+"FQLxLcLUYKDh7PT_1.1.F4.boolean.opBoolean","COPY",FACE,{"disambiguationData":[TD([subQ1])],"derivedFrom":subQ10})])],"derivedFrom":makeQuery(id+"FQLxLcLUYKDh7PT_1.1.F4.boolean.opBoolean","SPLIT",EDGE,{"disambiguationData":[TD([subQ13])],"derivedFrom":makeQuery(id+"F4.boolean.opBoolean","SPLIT",EDGE,{"disambiguationData":[TD([subQ13])],"derivedFrom":makeQuery(id+"F1.opExtrude","CAP_EDGE",EDGE,{"disambiguationData":[OSD([subQ0])],"isStart":true})})})});}
            var Q23;
            {var subQ0=sQuery(id+"F0.wireOp",EDGE,"E0");var subQ3=sQuery(id+"F0.wireOp",EDGE,"E3.right");var subQ4=sQuery(id+"F0.wireOp",EDGE,"E2");var subQ5=sQuery(id+"F0.wireOp",EDGE,"E1");var subQ7=sQuery(id+"F3.wireOp",EDGE,"E16");var subQ8=makeQuery(id+"FQLxLcLUYKDh7PT_1.2.F4.opExtrude","SWEPT_FACE",FACE,{"disambiguationData":[OSD([subQ7])]});var subQ9=makeQuery(id+"F0.imprint","INTERSECT",VERTEX,{"disambiguationData":[OD(1.0)],"derivedFrom":[subQ5,subQ4]});var subQ11=makeQuery(id+"F1.opExtrude","SWEPT_FACE",FACE,{"disambiguationData":[OSD([subQ4]),TDD([makeQuery(id+"F0.imprint","IMPRINT",EDGE,{"disambiguationData":[TD([[makeQuery(id+"F0.imprint","INTERSECT",VERTEX,{"derivedFrom":[subQ4,subQ3]}),-1.0]])],"derivedFrom":subQ4}),makeQuery(id+"F0.imprint","IMPRINT",EDGE,{"disambiguationData":[TD([[subQ9,1.0]])],"derivedFrom":subQ4}),makeQuery(id+"F0.imprint","IMPRINT",EDGE,{"disambiguationData":[TD([[makeQuery(id+"F0.imprint","INTERSECT",VERTEX,{"disambiguationData":[OD(1.0)],"derivedFrom":[subQ0,subQ4]}),1.0]])],"derivedFrom":subQ4})])]});Q23=makeQuery(id+"FQLxLcLUYKDh7PT_1.3.F4.boolean.opBoolean","SPLIT",EDGE,{"disambiguationData":[TD([makeQuery(id+"FQLxLcLUYKDh7PT_1.2.F4.boolean.opBoolean","COPY",FACE,{"derivedFrom":subQ8})])],"derivedFrom":makeQuery(id+"FQLxLcLUYKDh7PT_1.2.F4.boolean.opBoolean","SPLIT",EDGE,{"disambiguationData":[TD([subQ11])],"derivedFrom":makeQuery(id+"FQLxLcLUYKDh7PT_1.1.F4.boolean.opBoolean","SPLIT",EDGE,{"disambiguationData":[TD([subQ11])],"derivedFrom":makeQuery(id+"F4.boolean.opBoolean","SPLIT",EDGE,{"disambiguationData":[TD([subQ11])],"derivedFrom":makeQuery(id+"F1.opExtrude","CAP_EDGE",EDGE,{"disambiguationData":[OSD([subQ0])],"isStart":true})})})})});}
            var Q24;
            {var subQ0=sQuery(id+"F0.wireOp",EDGE,"E0");var subQ2=sQuery(id+"F3.wireOp",EDGE,"E16");var subQ3=makeQuery(id+"FQLxLcLUYKDh7PT_1.3.F4.opExtrude","SWEPT_FACE",FACE,{"disambiguationData":[OSD([subQ2])]});var subQ5=sQuery(id+"F0.wireOp",EDGE,"E3.right");var subQ6=sQuery(id+"F0.wireOp",EDGE,"E2");var subQ7=sQuery(id+"F0.wireOp",EDGE,"E1");var subQ9=makeQuery(id+"F0.imprint","INTERSECT",VERTEX,{"disambiguationData":[OD(1.0)],"derivedFrom":[subQ7,subQ6]});var subQ11=makeQuery(id+"F1.opExtrude","SWEPT_FACE",FACE,{"disambiguationData":[OSD([subQ6]),TDD([makeQuery(id+"F0.imprint","IMPRINT",EDGE,{"disambiguationData":[TD([[makeQuery(id+"F0.imprint","INTERSECT",VERTEX,{"derivedFrom":[subQ6,subQ5]}),-1.0]])],"derivedFrom":subQ6}),makeQuery(id+"F0.imprint","IMPRINT",EDGE,{"disambiguationData":[TD([[subQ9,1.0]])],"derivedFrom":subQ6}),makeQuery(id+"F0.imprint","IMPRINT",EDGE,{"disambiguationData":[TD([[makeQuery(id+"F0.imprint","INTERSECT",VERTEX,{"disambiguationData":[OD(1.0)],"derivedFrom":[subQ0,subQ6]}),1.0]])],"derivedFrom":subQ6})])]});Q24=makeQuery(id+"FQLxLcLUYKDh7PT_1.4.F4.boolean.opBoolean","SPLIT",EDGE,{"disambiguationData":[TD([makeQuery(id+"FQLxLcLUYKDh7PT_1.3.F4.boolean.opBoolean","COPY",FACE,{"derivedFrom":subQ3})])],"derivedFrom":makeQuery(id+"FQLxLcLUYKDh7PT_1.3.F4.boolean.opBoolean","SPLIT",EDGE,{"disambiguationData":[TD([subQ11])],"derivedFrom":makeQuery(id+"FQLxLcLUYKDh7PT_1.2.F4.boolean.opBoolean","SPLIT",EDGE,{"disambiguationData":[TD([subQ11])],"derivedFrom":makeQuery(id+"FQLxLcLUYKDh7PT_1.1.F4.boolean.opBoolean","SPLIT",EDGE,{"disambiguationData":[TD([subQ11])],"derivedFrom":makeQuery(id+"F4.boolean.opBoolean","SPLIT",EDGE,{"disambiguationData":[TD([subQ11])],"derivedFrom":makeQuery(id+"F1.opExtrude","CAP_EDGE",EDGE,{"disambiguationData":[OSD([subQ0])],"isStart":true})})})})})});}
            var Q25;
            {var subQ0=sQuery(id+"F0.wireOp",EDGE,"E0");var subQ3=sQuery(id+"F0.wireOp",EDGE,"E3.right");var subQ4=sQuery(id+"F0.wireOp",EDGE,"E2");var subQ5=sQuery(id+"F0.wireOp",EDGE,"E1");var subQ7=sQuery(id+"F3.wireOp",EDGE,"E16");var subQ8=makeQuery(id+"FQLxLcLUYKDh7PT_1.4.F4.opExtrude","SWEPT_FACE",FACE,{"disambiguationData":[OSD([subQ7])]});var subQ9=makeQuery(id+"F0.imprint","INTERSECT",VERTEX,{"disambiguationData":[OD(1.0)],"derivedFrom":[subQ5,subQ4]});var subQ11=makeQuery(id+"F1.opExtrude","SWEPT_FACE",FACE,{"disambiguationData":[OSD([subQ4]),TDD([makeQuery(id+"F0.imprint","IMPRINT",EDGE,{"disambiguationData":[TD([[makeQuery(id+"F0.imprint","INTERSECT",VERTEX,{"derivedFrom":[subQ4,subQ3]}),-1.0]])],"derivedFrom":subQ4}),makeQuery(id+"F0.imprint","IMPRINT",EDGE,{"disambiguationData":[TD([[subQ9,1.0]])],"derivedFrom":subQ4}),makeQuery(id+"F0.imprint","IMPRINT",EDGE,{"disambiguationData":[TD([[makeQuery(id+"F0.imprint","INTERSECT",VERTEX,{"disambiguationData":[OD(1.0)],"derivedFrom":[subQ0,subQ4]}),1.0]])],"derivedFrom":subQ4})])]});Q25=makeQuery(id+"FQLxLcLUYKDh7PT_1.5.F4.boolean.opBoolean","SPLIT",EDGE,{"disambiguationData":[TD([makeQuery(id+"FQLxLcLUYKDh7PT_1.4.F4.boolean.opBoolean","COPY",FACE,{"derivedFrom":subQ8})])],"derivedFrom":makeQuery(id+"FQLxLcLUYKDh7PT_1.4.F4.boolean.opBoolean","SPLIT",EDGE,{"disambiguationData":[TD([subQ11])],"derivedFrom":makeQuery(id+"FQLxLcLUYKDh7PT_1.3.F4.boolean.opBoolean","SPLIT",EDGE,{"disambiguationData":[TD([subQ11])],"derivedFrom":makeQuery(id+"FQLxLcLUYKDh7PT_1.2.F4.boolean.opBoolean","SPLIT",EDGE,{"disambiguationData":[TD([subQ11])],"derivedFrom":makeQuery(id+"FQLxLcLUYKDh7PT_1.1.F4.boolean.opBoolean","SPLIT",EDGE,{"disambiguationData":[TD([subQ11])],"derivedFrom":makeQuery(id+"F4.boolean.opBoolean","SPLIT",EDGE,{"disambiguationData":[TD([subQ11])],"derivedFrom":makeQuery(id+"F1.opExtrude","CAP_EDGE",EDGE,{"disambiguationData":[OSD([subQ0])],"isStart":true})})})})})})});}
            var Q26;
            {var subQ0=sQuery(id+"F0.wireOp",EDGE,"E0");var subQ3=sQuery(id+"F0.wireOp",EDGE,"E3.right");var subQ4=sQuery(id+"F0.wireOp",EDGE,"E2");var subQ5=sQuery(id+"F0.wireOp",EDGE,"E1");var subQ7=makeQuery(id+"F0.imprint","INTERSECT",VERTEX,{"disambiguationData":[OD(1.0)],"derivedFrom":[subQ5,subQ4]});var subQ9=makeQuery(id+"F1.opExtrude","SWEPT_FACE",FACE,{"disambiguationData":[OSD([subQ4]),TDD([makeQuery(id+"F0.imprint","IMPRINT",EDGE,{"disambiguationData":[TD([[makeQuery(id+"F0.imprint","INTERSECT",VERTEX,{"derivedFrom":[subQ4,subQ3]}),-1.0]])],"derivedFrom":subQ4}),makeQuery(id+"F0.imprint","IMPRINT",EDGE,{"disambiguationData":[TD([[subQ7,1.0]])],"derivedFrom":subQ4}),makeQuery(id+"F0.imprint","IMPRINT",EDGE,{"disambiguationData":[TD([[makeQuery(id+"F0.imprint","INTERSECT",VERTEX,{"disambiguationData":[OD(1.0)],"derivedFrom":[subQ0,subQ4]}),1.0]])],"derivedFrom":subQ4})])]});Q26=makeQuery(id+"FQLxLcLUYKDh7PT_1.5.F4.boolean.opBoolean","SPLIT",EDGE,{"disambiguationData":[TD([subQ9])],"derivedFrom":makeQuery(id+"FQLxLcLUYKDh7PT_1.4.F4.boolean.opBoolean","SPLIT",EDGE,{"disambiguationData":[TD([subQ9])],"derivedFrom":makeQuery(id+"FQLxLcLUYKDh7PT_1.3.F4.boolean.opBoolean","SPLIT",EDGE,{"disambiguationData":[TD([subQ9])],"derivedFrom":makeQuery(id+"FQLxLcLUYKDh7PT_1.2.F4.boolean.opBoolean","SPLIT",EDGE,{"disambiguationData":[TD([subQ9])],"derivedFrom":makeQuery(id+"FQLxLcLUYKDh7PT_1.1.F4.boolean.opBoolean","SPLIT",EDGE,{"disambiguationData":[TD([subQ9])],"derivedFrom":makeQuery(id+"F4.boolean.opBoolean","SPLIT",EDGE,{"disambiguationData":[TD([subQ9])],"derivedFrom":makeQuery(id+"F1.opExtrude","CAP_EDGE",EDGE,{"disambiguationData":[OSD([subQ0])],"isStart":true})})})})})})});}
            var Q27;
            {var subQ0=sQuery(id+"F0.wireOp",EDGE,"E1");Q27=makeQuery(id+"F5.boolean.opBoolean","COPY",EDGE,{"derivedFrom":makeQuery(id+"F5.opExtrude","CAP_EDGE",EDGE,{"disambiguationData":[OSD([subQ0]),TDD([makeQuery(id+"F0.imprint","IMPRINT",EDGE,{"disambiguationData":[TD([[makeQuery(id+"F0.imprint","INTERSECT",VERTEX,{"derivedFrom":[subQ0,sQuery(id+"F0.wireOp",EDGE,"E13.MirrorCS")]}),-1.0]])],"derivedFrom":subQ0})])],"isStart":true})});}
            var Q28;
            {var subQ0=sQuery(id+"F0.wireOp",EDGE,"E1");Q28=makeQuery(id+"F1.opExtrude","CAP_EDGE",EDGE,{"disambiguationData":[OSD([subQ0]),TDD([makeQuery(id+"F0.imprint","IMPRINT",EDGE,{"disambiguationData":[TD([[makeQuery(id+"F0.imprint","INTERSECT",VERTEX,{"derivedFrom":[subQ0,sQuery(id+"F0.wireOp",EDGE,"E12.MirrorCS")]}),-1.0]])],"derivedFrom":subQ0})])],"isStart":true});}
            var Q29;
            {var subQ0=sQuery(id+"F0.wireOp",EDGE,"E1");Q29=makeQuery(id+"F5.boolean.opBoolean","COPY",EDGE,{"derivedFrom":makeQuery(id+"F5.opExtrude","CAP_EDGE",EDGE,{"disambiguationData":[OSD([subQ0]),TDD([makeQuery(id+"F0.imprint","IMPRINT",EDGE,{"disambiguationData":[TD([[makeQuery(id+"F0.imprint","INTERSECT",VERTEX,{"derivedFrom":[subQ0,sQuery(id+"F0.wireOp",EDGE,"E11.MirrorCS")]}),-1.0]])],"derivedFrom":subQ0})])],"isStart":true})});}
            var Q30;
            {var subQ1=sQuery(id+"F0.wireOp",EDGE,"E11.MirrorCS");var subQ2=sQuery(id+"F0.wireOp",EDGE,"E1");var subQ4=makeQuery(id+"F0.imprint","IMPRINT",EDGE,{"disambiguationData":[TD([[makeQuery(id+"F0.imprint","INTERSECT",VERTEX,{"derivedFrom":[subQ2,subQ1]}),1.0]])],"derivedFrom":subQ2});var subQ6=makeQuery(id+"F1.opExtrude","SWEPT_FACE",FACE,{"disambiguationData":[OSD([subQ1])]});Q30=makeQuery(id+"FQLxLcLUYKDh7PT_1.2.F4.boolean.opBoolean","SPLIT",EDGE,{"disambiguationData":[TD([subQ6])],"derivedFrom":makeQuery(id+"FQLxLcLUYKDh7PT_1.1.F4.boolean.opBoolean","SPLIT",EDGE,{"disambiguationData":[TD([subQ6])],"derivedFrom":makeQuery(id+"F1.opExtrude","CAP_EDGE",EDGE,{"disambiguationData":[OSD([subQ2]),TDD([subQ4])],"isStart":true})})});}
            var Q31;
            {var subQ1=sQuery(id+"F0.wireOp",EDGE,"E11.MirrorCS");var subQ2=sQuery(id+"F0.wireOp",EDGE,"E1");var subQ3=sQuery(id+"F0.wireOp",EDGE,"E0");var subQ5=makeQuery(id+"F0.imprint","IMPRINT",EDGE,{"disambiguationData":[TD([[makeQuery(id+"F0.imprint","INTERSECT",VERTEX,{"derivedFrom":[subQ2,subQ1]}),1.0]])],"derivedFrom":subQ2});var subQ7=sQuery(id+"F3.wireOp",EDGE,"E16");var subQ8=makeQuery(id+"FQLxLcLUYKDh7PT_1.1.F4.opExtrude","SWEPT_FACE",FACE,{"disambiguationData":[OSD([subQ7])]});Q31=makeQuery(id+"FQLxLcLUYKDh7PT_1.2.F4.boolean.opBoolean","SPLIT",EDGE,{"disambiguationData":[TD([makeQuery(id+"FQLxLcLUYKDh7PT_1.1.F4.boolean.opBoolean","COPY",FACE,{"disambiguationData":[TD([makeQuery(id+"F1.opExtrude","SWEPT_FACE",FACE,{"disambiguationData":[OSD([subQ3])]})])],"derivedFrom":subQ8})])],"derivedFrom":makeQuery(id+"FQLxLcLUYKDh7PT_1.1.F4.boolean.opBoolean","SPLIT",EDGE,{"disambiguationData":[TD([makeQuery(id+"F1.opExtrude","SWEPT_FACE",FACE,{"disambiguationData":[OSD([subQ1])]})])],"derivedFrom":makeQuery(id+"F1.opExtrude","CAP_EDGE",EDGE,{"disambiguationData":[OSD([subQ2]),TDD([subQ5])],"isStart":true})})});}
            var Q32;
            {var subQ0=sQuery(id+"F0.wireOp",EDGE,"E14");var subQ1=sQuery(id+"F0.wireOp",EDGE,"E1");var subQ2=sQuery(id+"F0.wireOp",EDGE,"E15.MirrorCS");var subQ4=sQuery(id+"F0.wireOp",EDGE,"E11.MirrorCS");var subQ5=makeQuery(id+"F0.imprint","IMPRINT",EDGE,{"disambiguationData":[TD([[makeQuery(id+"F0.imprint","INTERSECT",VERTEX,{"derivedFrom":[subQ1,subQ4]}),1.0]])],"derivedFrom":subQ1});Q32=makeQuery(id+"F5.boolean.opBoolean","MERGE",EDGE,{"derivedFrom":[makeQuery(id+"FQLxLcLUYKDh7PT_1.1.F4.boolean.opBoolean","SPLIT",EDGE,{"disambiguationData":[TD([makeQuery(id+"F1.opExtrude","SWEPT_FACE",FACE,{"disambiguationData":[OSD([subQ2])]})])],"derivedFrom":makeQuery(id+"F1.opExtrude","CAP_EDGE",EDGE,{"disambiguationData":[OSD([subQ1]),TDD([subQ5])],"isStart":true})}),makeQuery(id+"F5.opExtrude","CAP_EDGE",EDGE,{"disambiguationData":[OSD([subQ1]),TDD([makeQuery(id+"F0.imprint","IMPRINT",EDGE,{"disambiguationData":[TD([[makeQuery(id+"F0.imprint","INTERSECT",VERTEX,{"derivedFrom":[subQ1,subQ0]}),-1.0]])],"derivedFrom":subQ1})])],"isStart":true})]});}
            var Q33;
            {var subQ0=sQuery(id+"F0.wireOp",EDGE,"E14");var subQ1=sQuery(id+"F0.wireOp",EDGE,"E1");var subQ2=makeQuery(id+"F0.imprint","INTERSECT",VERTEX,{"derivedFrom":[subQ1,subQ0]});var subQ4=sQuery(id+"F0.wireOp",EDGE,"E9");var subQ6=makeQuery(id+"F0.imprint","IMPRINT",EDGE,{"disambiguationData":[TD([[makeQuery(id+"F0.imprint","INTERSECT",VERTEX,{"derivedFrom":[subQ1,subQ4]}),-1.0]])],"derivedFrom":subQ1});var subQ8=makeQuery(id+"F1.opExtrude","SWEPT_FACE",FACE,{"disambiguationData":[OSD([subQ0])]});Q33=makeQuery(id+"F5.boolean.opBoolean","MERGE",EDGE,{"derivedFrom":[makeQuery(id+"FQLxLcLUYKDh7PT_1.-1.F4.boolean.opBoolean","SPLIT",EDGE,{"disambiguationData":[TD([subQ8])],"derivedFrom":makeQuery(id+"FQLxLcLUYKDh7PT_1.-2.F4.boolean.opBoolean","SPLIT",EDGE,{"disambiguationData":[TD([subQ8])],"derivedFrom":makeQuery(id+"F1.opExtrude","CAP_EDGE",EDGE,{"disambiguationData":[OSD([subQ1]),TDD([subQ6])],"isStart":true})})}),makeQuery(id+"F5.opExtrude","CAP_EDGE",EDGE,{"disambiguationData":[OSD([subQ1]),TDD([makeQuery(id+"F0.imprint","IMPRINT",EDGE,{"disambiguationData":[TD([[subQ2,-1.0]])],"derivedFrom":subQ1})])],"isStart":true})]});}
            var Q34;
            {var subQ0=sQuery(id+"F0.wireOp",EDGE,"E14");var subQ1=sQuery(id+"F0.wireOp",EDGE,"E9");var subQ2=sQuery(id+"F0.wireOp",EDGE,"E1");var subQ4=makeQuery(id+"F0.imprint","IMPRINT",EDGE,{"disambiguationData":[TD([[makeQuery(id+"F0.imprint","INTERSECT",VERTEX,{"derivedFrom":[subQ2,subQ1]}),-1.0]])],"derivedFrom":subQ2});var subQ6=sQuery(id+"F3.wireOp",EDGE,"E16");var subQ7=makeQuery(id+"FQLxLcLUYKDh7PT_1.-2.F4.opExtrude","SWEPT_FACE",FACE,{"disambiguationData":[OSD([subQ6])]});Q34=makeQuery(id+"FQLxLcLUYKDh7PT_1.-1.F4.boolean.opBoolean","SPLIT",EDGE,{"disambiguationData":[TD([makeQuery(id+"FQLxLcLUYKDh7PT_1.-2.F4.boolean.opBoolean","COPY",FACE,{"derivedFrom":subQ7})])],"derivedFrom":makeQuery(id+"FQLxLcLUYKDh7PT_1.-2.F4.boolean.opBoolean","SPLIT",EDGE,{"disambiguationData":[TD([makeQuery(id+"F1.opExtrude","SWEPT_FACE",FACE,{"disambiguationData":[OSD([subQ0])]})])],"derivedFrom":makeQuery(id+"F1.opExtrude","CAP_EDGE",EDGE,{"disambiguationData":[OSD([subQ2]),TDD([subQ4])],"isStart":true})})});}
            var Q35;
            {var subQ1=sQuery(id+"F0.wireOp",EDGE,"E9");var subQ2=sQuery(id+"F0.wireOp",EDGE,"E1");var subQ3=sQuery(id+"F3.wireOp",EDGE,"E16");var subQ4=makeQuery(id+"F0.imprint","IMPRINT",EDGE,{"disambiguationData":[TD([[makeQuery(id+"F0.imprint","INTERSECT",VERTEX,{"derivedFrom":[subQ2,subQ1]}),-1.0]])],"derivedFrom":subQ2});Q35=makeQuery(id+"FQLxLcLUYKDh7PT_1.-2.F4.boolean.opBoolean","SPLIT",EDGE,{"disambiguationData":[TD([makeQuery(id+"FQLxLcLUYKDh7PT_1.-3.F4.boolean.opBoolean","COPY",FACE,{"derivedFrom":makeQuery(id+"FQLxLcLUYKDh7PT_1.-3.F4.opExtrude","SWEPT_FACE",FACE,{"disambiguationData":[OSD([subQ3])]})})])],"derivedFrom":makeQuery(id+"F1.opExtrude","CAP_EDGE",EDGE,{"disambiguationData":[OSD([subQ2]),TDD([subQ4])],"isStart":true})});}
            var Q36;
            {var subQ0=sQuery(id+"F0.wireOp",EDGE,"E1");Q36=makeQuery(id+"F5.boolean.opBoolean","COPY",EDGE,{"derivedFrom":makeQuery(id+"F5.opExtrude","CAP_EDGE",EDGE,{"disambiguationData":[OSD([subQ0]),TDD([makeQuery(id+"F0.imprint","IMPRINT",EDGE,{"disambiguationData":[TD([[makeQuery(id+"F0.imprint","INTERSECT",VERTEX,{"derivedFrom":[subQ0,sQuery(id+"F0.wireOp",EDGE,"E7")]}),-1.0]])],"derivedFrom":subQ0})])],"isStart":true})});}
            var Q37;
            {var subQ0=sQuery(id+"F0.wireOp",EDGE,"E1");Q37=makeQuery(id+"F1.opExtrude","CAP_EDGE",EDGE,{"disambiguationData":[OSD([subQ0]),TDD([makeQuery(id+"F0.imprint","IMPRINT",EDGE,{"disambiguationData":[TD([[makeQuery(id+"F0.imprint","INTERSECT",VERTEX,{"derivedFrom":[subQ0,sQuery(id+"F0.wireOp",EDGE,"E4")]}),-1.0]])],"derivedFrom":subQ0})])],"isStart":true});}
            var Q38;
            {var subQ0=sQuery(id+"F0.wireOp",EDGE,"E1");Q38=makeQuery(id+"F5.boolean.opBoolean","COPY",EDGE,{"derivedFrom":makeQuery(id+"F5.opExtrude","CAP_EDGE",EDGE,{"disambiguationData":[OSD([subQ0]),TDD([makeQuery(id+"F0.imprint","IMPRINT",EDGE,{"disambiguationData":[TD([[makeQuery(id+"F0.imprint","INTERSECT",VERTEX,{"derivedFrom":[subQ0,sQuery(id+"F0.wireOp",EDGE,"E4")]}),1.0]])],"derivedFrom":subQ0})])],"isStart":true})});}
            fillet(context, id + "F6", {"entities" : qUnion([Q0, Q1, Q2, Q3, Q4, Q5, Q6, Q7, Q8, Q9, Q10, Q11, Q12, Q13, Q14, Q15, Q16, Q17, Q18, Q19, Q20, Q21, Q22, Q23, Q24, Q25, Q26, Q27, Q28, Q29, Q30, Q31, Q32, Q33, Q34, Q35, Q36, Q37, Q38]), "radius" : 5.08 * mm, "tangentPropagation" : true, "allowEdgeOverflow" : false});
        }
        {
            var Q0;
            Q0=makeQuery(id+"F1.opExtrude","CAP_EDGE",EDGE,{"disambiguationData":[OSD([sQuery(id+"F0.wireOp",EDGE,"E0")])],"isStart":false});
            fillet(context, id + "F7", {"entities" : qUnion([Q0]), "radius" : 19.05 * mm, "tangentPropagation" : true, "allowEdgeOverflow" : false});
        }
        {
            var Q0;
            Q0=makeQuery(id+"F1.opExtrude","SWEPT_FACE",FACE,{"disambiguationData":[OSD([sQuery(id+"F0.wireOp",EDGE,"E10.right")])]});
            var Q1;
            Q1=makeQuery(id+"F1.opExtrude","SWEPT_FACE",FACE,{"disambiguationData":[OSD([sQuery(id+"F0.wireOp",EDGE,"E10.left")])]});
            var Q2;
            {var subQ0=sQuery(id+"F0.wireOp",EDGE,"E10.bottom");Q2=makeQuery(id+"F1.opExtrude","SWEPT_FACE",FACE,{"disambiguationData":[OSD([subQ0]),TDD([makeQuery(id+"F0.imprint","IMPRINT",EDGE,{"disambiguationData":[TD([[makeQuery(id+"F0.imprint","INTERSECT",VERTEX,{"derivedFrom":[subQ0,sQuery(id+"F0.wireOp",EDGE,"E14")]}),1.0]])],"derivedFrom":subQ0})])]});}
            var Q3;
            {var subQ0=sQuery(id+"F0.wireOp",EDGE,"E10.bottom");Q3=makeQuery(id+"F1.opExtrude","SWEPT_FACE",FACE,{"disambiguationData":[OSD([subQ0]),TDD([makeQuery(id+"F0.imprint","IMPRINT",EDGE,{"disambiguationData":[TD([[makeQuery(id+"F0.imprint","INTERSECT",VERTEX,{"derivedFrom":[subQ0,sQuery(id+"F0.wireOp",EDGE,"E15.MirrorCS")]}),-1.0]])],"derivedFrom":subQ0})])]});}
            var Q4;
            {var subQ0=sQuery(id+"F0.wireOp",EDGE,"E1");Q4=makeQuery(id+"F1.opExtrude","CAP_EDGE",EDGE,{"disambiguationData":[OSD([subQ0]),TDD([makeQuery(id+"F0.imprint","IMPRINT",EDGE,{"disambiguationData":[TD([[makeQuery(id+"F0.imprint","INTERSECT",VERTEX,{"derivedFrom":[subQ0,sQuery(id+"F0.wireOp",EDGE,"E4")]}),-1.0]])],"derivedFrom":subQ0})])],"isStart":false});}
            var Q5;
            {var subQ0=sQuery(id+"F0.wireOp",EDGE,"E1");Q5=makeQuery(id+"F1.opExtrude","CAP_EDGE",EDGE,{"disambiguationData":[OSD([subQ0]),TDD([makeQuery(id+"F0.imprint","IMPRINT",EDGE,{"disambiguationData":[TD([[makeQuery(id+"F0.imprint","INTERSECT",VERTEX,{"derivedFrom":[subQ0,sQuery(id+"F0.wireOp",EDGE,"E9")]}),-1.0]])],"derivedFrom":subQ0})])],"isStart":false});}
            var Q6;
            {var subQ0=sQuery(id+"F0.wireOp",EDGE,"E1");Q6=makeQuery(id+"F1.opExtrude","CAP_EDGE",EDGE,{"disambiguationData":[OSD([subQ0]),TDD([makeQuery(id+"F0.imprint","IMPRINT",EDGE,{"disambiguationData":[TD([[makeQuery(id+"F0.imprint","INTERSECT",VERTEX,{"derivedFrom":[subQ0,sQuery(id+"F0.wireOp",EDGE,"E11.MirrorCS")]}),1.0]])],"derivedFrom":subQ0})])],"isStart":false});}
            var Q7;
            {var subQ0=sQuery(id+"F0.wireOp",EDGE,"E1");Q7=makeQuery(id+"F1.opExtrude","CAP_EDGE",EDGE,{"disambiguationData":[OSD([subQ0]),TDD([makeQuery(id+"F0.imprint","IMPRINT",EDGE,{"disambiguationData":[TD([[makeQuery(id+"F0.imprint","INTERSECT",VERTEX,{"derivedFrom":[subQ0,sQuery(id+"F0.wireOp",EDGE,"E12.MirrorCS")]}),-1.0]])],"derivedFrom":subQ0})])],"isStart":false});}
            fillet(context, id + "F8", {"entities" : qUnion([Q0, Q1, Q2, Q3, Q4, Q5, Q6, Q7]), "radius" : 6.35 * mm, "tangentPropagation" : true, "allowEdgeOverflow" : false});
        }
        {
            var Q0;
            Q0=makeQuery(id+"F1.opExtrude","SWEPT_EDGE",EDGE,{"disambiguationData":[OSD([sQuery(id+"F0.wireOp",EDGE,"E1"),sQuery(id+"F0.wireOp",EDGE,"E15.MirrorCS")])]});
            var Q1;
            Q1=makeQuery(id+"F1.opExtrude","SWEPT_EDGE",EDGE,{"disambiguationData":[OSD([sQuery(id+"F0.wireOp",EDGE,"E1"),sQuery(id+"F0.wireOp",EDGE,"E11.MirrorCS")])]});
            var Q2;
            Q2=makeQuery(id+"F1.opExtrude","SWEPT_EDGE",EDGE,{"disambiguationData":[OSD([sQuery(id+"F0.wireOp",EDGE,"E1"),sQuery(id+"F0.wireOp",EDGE,"E13.MirrorCS")])]});
            var Q3;
            Q3=makeQuery(id+"F1.opExtrude","SWEPT_EDGE",EDGE,{"disambiguationData":[OSD([sQuery(id+"F0.wireOp",EDGE,"E1"),sQuery(id+"F0.wireOp",EDGE,"E14")])]});
            var Q4;
            Q4=makeQuery(id+"F1.opExtrude","SWEPT_EDGE",EDGE,{"disambiguationData":[OSD([sQuery(id+"F0.wireOp",EDGE,"E1"),sQuery(id+"F0.wireOp",EDGE,"E9")])]});
            var Q5;
            Q5=makeQuery(id+"F1.opExtrude","SWEPT_EDGE",EDGE,{"disambiguationData":[OSD([sQuery(id+"F0.wireOp",EDGE,"E1"),sQuery(id+"F0.wireOp",EDGE,"E4")])]});
            fillet(context, id + "F9", {"entities" : qUnion([Q0, Q1, Q2, Q3, Q4, Q5]), "radius" : 5.33 * mm, "tangentPropagation" : true, "allowEdgeOverflow" : false});
        }
        {
            var Q0;
            Q0=makeQuery(id+"F1.opExtrude","CAP_FACE",FACE,{"disambiguationData":[OSD([sQuery(id+"F0.wireOp",EDGE,"E0"),sQuery(id+"F0.wireOp",EDGE,"E1"),sQuery(id+"F0.wireOp",EDGE,"E2"),sQuery(id+"F0.wireOp",EDGE,"E3.bottom"),sQuery(id+"F0.wireOp",EDGE,"E3.left"),sQuery(id+"F0.wireOp",EDGE,"E3.right"),sQuery(id+"F0.wireOp",EDGE,"E4"),sQuery(id+"F0.wireOp",EDGE,"E7"),sQuery(id+"F0.wireOp",EDGE,"E9"),sQuery(id+"F0.wireOp",EDGE,"E10.bottom"),sQuery(id+"F0.wireOp",EDGE,"E10.left"),sQuery(id+"F0.wireOp",EDGE,"E10.right"),sQuery(id+"F0.wireOp",EDGE,"E11.MirrorCS"),sQuery(id+"F0.wireOp",EDGE,"E12.MirrorCS"),sQuery(id+"F0.wireOp",EDGE,"E13.MirrorCS"),sQuery(id+"F0.wireOp",EDGE,"E14"),sQuery(id+"F0.wireOp",EDGE,"E15.MirrorCS")])],"isStart":false});
            var sketch = newSketch(context, id + "F10", { "sketchPlane" : qUnion([Q0])});
            skCircle(sketch, "E17", {"center": v(0, -38.35) * mm, "radius": 7.94 * mm});
            skCircle(sketch, "E18.1.0.0", {"center": v(0, -61.6) * mm, "radius": 7.94 * mm});
            skCircle(sketch, "E18.2.0.0", {"center": v(0, -84.84) * mm, "radius": 7.94 * mm});
            skCircle(sketch, "E18.3.0.0", {"center": v(0, -108.08) * mm, "radius": 7.94 * mm});
            skLineSegment(sketch, "E18.direction1", {"start": v(0, -38.35) * mm, "end": v(0, -61.6) * mm, "construction": true});
            skSolve(sketch);
        }
        {
            var Q0;
            Q0=makeQuery(id+"F10.imprint","IMPRINT",FACE,{"disambiguationData":[TD([[makeQuery(id+"F10.imprint","IMPRINT",EDGE,{"derivedFrom":sQuery(id+"F10.wireOp",EDGE,"E17")}),1.0]])]});
            var Q1;
            Q1=makeQuery(id+"F10.imprint","IMPRINT",FACE,{"disambiguationData":[TD([[makeQuery(id+"F10.imprint","IMPRINT",EDGE,{"derivedFrom":sQuery(id+"F10.wireOp",EDGE,"E18.1.0.0")}),1.0]])]});
            var Q2;
            Q2=makeQuery(id+"F10.imprint","IMPRINT",FACE,{"disambiguationData":[TD([[makeQuery(id+"F10.imprint","IMPRINT",EDGE,{"derivedFrom":sQuery(id+"F10.wireOp",EDGE,"E18.2.0.0")}),1.0]])]});
            var Q3;
            {var subQ0=sQuery(id+"F10.wireOp",EDGE,"E18.3.0.0");var subQ1=sQuery(id+"F0.wireOp",EDGE,"E0");var subQ2=makeQuery(id+"F7.opFillet","BLEND_EDGE",EDGE,{"blendedFrom":[makeQuery(id+"F1.opExtrude","CAP_EDGE",EDGE,{"disambiguationData":[OSD([subQ1])],"isStart":false}),makeQuery(id+"F1.opExtrude","CAP_FACE",FACE,{"disambiguationData":[OSD([subQ1,sQuery(id+"F0.wireOp",EDGE,"E1"),sQuery(id+"F0.wireOp",EDGE,"E2"),sQuery(id+"F0.wireOp",EDGE,"E3.bottom"),sQuery(id+"F0.wireOp",EDGE,"E3.left"),sQuery(id+"F0.wireOp",EDGE,"E3.right"),sQuery(id+"F0.wireOp",EDGE,"E4"),sQuery(id+"F0.wireOp",EDGE,"E7"),sQuery(id+"F0.wireOp",EDGE,"E9"),sQuery(id+"F0.wireOp",EDGE,"E10.bottom"),sQuery(id+"F0.wireOp",EDGE,"E10.left"),sQuery(id+"F0.wireOp",EDGE,"E10.right"),sQuery(id+"F0.wireOp",EDGE,"E11.MirrorCS"),sQuery(id+"F0.wireOp",EDGE,"E12.MirrorCS"),sQuery(id+"F0.wireOp",EDGE,"E13.MirrorCS"),sQuery(id+"F0.wireOp",EDGE,"E14"),sQuery(id+"F0.wireOp",EDGE,"E15.MirrorCS")])],"isStart":false})],"blendedInto":[makeQuery(id+"F1.opExtrude","CAP_FACE",FACE,{"disambiguationData":[OSD([subQ1,sQuery(id+"F0.wireOp",EDGE,"E1"),sQuery(id+"F0.wireOp",EDGE,"E2"),sQuery(id+"F0.wireOp",EDGE,"E3.bottom"),sQuery(id+"F0.wireOp",EDGE,"E3.left"),sQuery(id+"F0.wireOp",EDGE,"E3.right"),sQuery(id+"F0.wireOp",EDGE,"E4"),sQuery(id+"F0.wireOp",EDGE,"E7"),sQuery(id+"F0.wireOp",EDGE,"E9"),sQuery(id+"F0.wireOp",EDGE,"E10.bottom"),sQuery(id+"F0.wireOp",EDGE,"E10.left"),sQuery(id+"F0.wireOp",EDGE,"E10.right"),sQuery(id+"F0.wireOp",EDGE,"E11.MirrorCS"),sQuery(id+"F0.wireOp",EDGE,"E12.MirrorCS"),sQuery(id+"F0.wireOp",EDGE,"E13.MirrorCS"),sQuery(id+"F0.wireOp",EDGE,"E14"),sQuery(id+"F0.wireOp",EDGE,"E15.MirrorCS")])],"isStart":false})]});var subQ3=makeQuery(id+"F10.imprint","INTERSECT",VERTEX,{"disambiguationData":[OD(0.0)],"derivedFrom":[subQ2,subQ0]});Q3=makeQuery(id+"F10.imprint","IMPRINT",FACE,{"disambiguationData":[TD([[makeQuery(id+"F10.imprint","IMPRINT",EDGE,{"disambiguationData":[TD([[subQ3,1.0]])],"derivedFrom":subQ0}),1.0]])]});}
            var Q4;
            {var subQ0=sQuery(id+"F10.wireOp",EDGE,"E18.3.0.0");var subQ1=sQuery(id+"F0.wireOp",EDGE,"E0");var subQ2=makeQuery(id+"F7.opFillet","BLEND_EDGE",EDGE,{"blendedFrom":[makeQuery(id+"F1.opExtrude","CAP_EDGE",EDGE,{"disambiguationData":[OSD([subQ1])],"isStart":false}),makeQuery(id+"F1.opExtrude","CAP_FACE",FACE,{"disambiguationData":[OSD([subQ1,sQuery(id+"F0.wireOp",EDGE,"E1"),sQuery(id+"F0.wireOp",EDGE,"E2"),sQuery(id+"F0.wireOp",EDGE,"E3.bottom"),sQuery(id+"F0.wireOp",EDGE,"E3.left"),sQuery(id+"F0.wireOp",EDGE,"E3.right"),sQuery(id+"F0.wireOp",EDGE,"E4"),sQuery(id+"F0.wireOp",EDGE,"E7"),sQuery(id+"F0.wireOp",EDGE,"E9"),sQuery(id+"F0.wireOp",EDGE,"E10.bottom"),sQuery(id+"F0.wireOp",EDGE,"E10.left"),sQuery(id+"F0.wireOp",EDGE,"E10.right"),sQuery(id+"F0.wireOp",EDGE,"E11.MirrorCS"),sQuery(id+"F0.wireOp",EDGE,"E12.MirrorCS"),sQuery(id+"F0.wireOp",EDGE,"E13.MirrorCS"),sQuery(id+"F0.wireOp",EDGE,"E14"),sQuery(id+"F0.wireOp",EDGE,"E15.MirrorCS")])],"isStart":false})],"blendedInto":[makeQuery(id+"F1.opExtrude","CAP_FACE",FACE,{"disambiguationData":[OSD([subQ1,sQuery(id+"F0.wireOp",EDGE,"E1"),sQuery(id+"F0.wireOp",EDGE,"E2"),sQuery(id+"F0.wireOp",EDGE,"E3.bottom"),sQuery(id+"F0.wireOp",EDGE,"E3.left"),sQuery(id+"F0.wireOp",EDGE,"E3.right"),sQuery(id+"F0.wireOp",EDGE,"E4"),sQuery(id+"F0.wireOp",EDGE,"E7"),sQuery(id+"F0.wireOp",EDGE,"E9"),sQuery(id+"F0.wireOp",EDGE,"E10.bottom"),sQuery(id+"F0.wireOp",EDGE,"E10.left"),sQuery(id+"F0.wireOp",EDGE,"E10.right"),sQuery(id+"F0.wireOp",EDGE,"E11.MirrorCS"),sQuery(id+"F0.wireOp",EDGE,"E12.MirrorCS"),sQuery(id+"F0.wireOp",EDGE,"E13.MirrorCS"),sQuery(id+"F0.wireOp",EDGE,"E14"),sQuery(id+"F0.wireOp",EDGE,"E15.MirrorCS")])],"isStart":false})]});var subQ3=makeQuery(id+"F10.imprint","INTERSECT",VERTEX,{"disambiguationData":[OD(0.0)],"derivedFrom":[subQ2,subQ0]});Q4=makeQuery(id+"F10.imprint","IMPRINT",FACE,{"disambiguationData":[TD([[makeQuery(id+"F10.imprint","IMPRINT",EDGE,{"disambiguationData":[TD([[subQ3,-1.0]])],"derivedFrom":subQ0}),1.0]])]});}
            extrude(context, id + "F11", {"entities" : qUnion([Q0, Q1, Q2, Q3, Q4]), "operationType" : NewBodyOperationType.REMOVE, "endBound" : BoundingType.THROUGH_ALL, "oppositeDirection" : true, "depth" : 25.4 * mm, "offsetDistance" : 25.4 * mm});
        }
        {
            var Q0;
            Q0=makeQuery(id+"F11.boolean.opBoolean","COPY",FACE,{"derivedFrom":makeQuery(id+"F11.opExtrude","SWEPT_FACE",FACE,{"disambiguationData":[OSD([sQuery(id+"F10.wireOp",EDGE,"E17")])]})});
            var Q1;
            Q1=makeQuery(id+"F11.boolean.opBoolean","COPY",FACE,{"derivedFrom":makeQuery(id+"F11.opExtrude","SWEPT_FACE",FACE,{"disambiguationData":[OSD([sQuery(id+"F10.wireOp",EDGE,"E18.1.0.0")])]})});
            var Q2;
            Q2=makeQuery(id+"F11.boolean.opBoolean","COPY",FACE,{"derivedFrom":makeQuery(id+"F11.opExtrude","SWEPT_FACE",FACE,{"disambiguationData":[OSD([sQuery(id+"F10.wireOp",EDGE,"E18.2.0.0")])]})});
            var Q3;
            Q3=makeQuery(id+"F11.boolean.opBoolean","COPY",FACE,{"derivedFrom":makeQuery(id+"F11.opExtrude","SWEPT_FACE",FACE,{"disambiguationData":[OSD([sQuery(id+"F10.wireOp",EDGE,"E18.3.0.0")])]})});
            fillet(context, id + "F12", {"entities" : qUnion([Q0, Q1, Q2, Q3]), "radius" : 5.08 * mm, "tangentPropagation" : true, "allowEdgeOverflow" : false});
        }
    });
